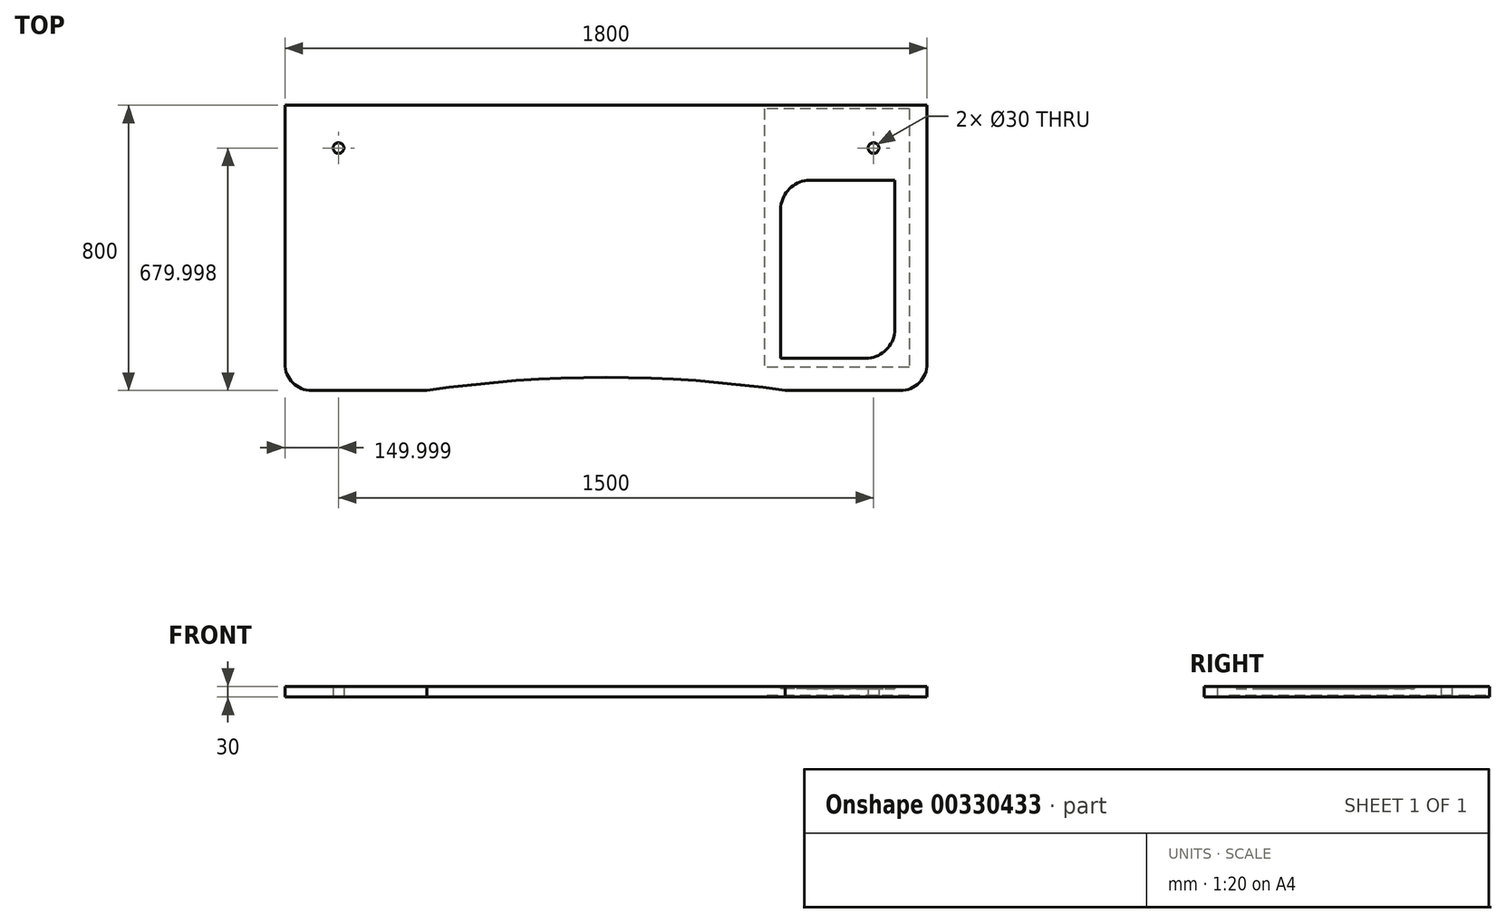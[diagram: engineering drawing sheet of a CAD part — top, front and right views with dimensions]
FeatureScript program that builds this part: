
annotation { "Feature Type Name" : "Feature", "Feature Type Description" : "" }
export const myFeature = defineFeature(function(context is Context, id is Id, definition is map)
    precondition{}
    {
        {
            var Q0;
            Q0=qCreatedBy(makeId("Top.planeOp"),FACE);
            var sketch = newSketch(context, id + "F0", { "sketchPlane" : qUnion([Q0])});
            skLineSegment(sketch, "E0.bottom", {"start": v(4430.2, -369.52) * mm, "end": v(4753.06, -369.52) * mm});
            skLineSegment(sketch, "E0.top", {"start": v(4355.2, 430.48) * mm, "end": v(6155.2, 430.48) * mm});
            skLineSegment(sketch, "E0.left", {"start": v(4355.2, -294.52) * mm, "end": v(4355.2, 430.48) * mm});
            skLineSegment(sketch, "E0.right", {"start": v(6155.2, -294.52) * mm, "end": v(6155.2, 430.48) * mm});
            skPoint(sketch, "E0.middle", {"position": v(5255.2, 30.48) * mm});
            skPoint(sketch, "E1.visualSharp", {"position": v(4355.2, -369.52) * mm});
            skArc(sketch, "E1.filletArc", {"start": v(4355.2, -294.52) * mm, "mid": v(4377.17, -347.55) * mm, "end": v(4430.2, -369.52) * mm});
            skPoint(sketch, "E2.visualSharp", {"position": v(6155.2, -369.52) * mm});
            skArc(sketch, "E2.filletArc", {"start": v(6080.2, -369.52) * mm, "mid": v(6133.23, -347.55) * mm, "end": v(6155.2, -294.52) * mm});
            skPoint(sketch, "E3", {"position": v(6155.2, 67.98) * mm});
            skLineSegment(sketch, "E4", {"start": v(6065.2, -195.15) * mm, "end": v(6065.2, 163.36) * mm});
            skLineSegment(sketch, "E5.3", {"start": v(6055.2, -204.44) * mm, "end": v(6055.2, 210.56) * mm});
            skPoint(sketch, "E6", {"position": v(4355.2, 310.48) * mm});
            skPoint(sketch, "E7", {"position": v(4505.2, 310.48) * mm});
            skLineSegment(sketch, "E8", {"start": v(5255.2, 30.48) * mm, "end": v(5255.2, 243.64) * mm, "construction": true});
            skCircle(sketch, "E9", {"center": v(4505.2, 310.48) * mm, "radius": 15 * mm});
            skCircle(sketch, "E10.MirrorC", {"center": v(6005.2, 310.48) * mm, "radius": 15 * mm});
            skLineSegment(sketch, "E11", {"start": v(5968, -279.52) * mm, "end": v(5990.2, -279.5) * mm});
            skLineSegment(sketch, "E12", {"start": v(6065.2, -204.44) * mm, "end": v(6065.2, -195.15) * mm});
            skPoint(sketch, "E13", {"position": v(6065.2, -204.44) * mm});
            skPoint(sketch, "E14", {"position": v(5990.2, -279.5) * mm});
            skPoint(sketch, "E15", {"position": v(5990.2, -269.22) * mm});
            skPoint(sketch, "E16", {"position": v(6055.2, -204.44) * mm});
            skPoint(sketch, "E17.orphan", {"position": v(6065.2, -279.44) * mm});
            skPoint(sketch, "E18", {"position": v(5755.2, -269.44) * mm});
            skLineSegment(sketch, "E19", {"start": v(5755.2, -269.44) * mm, "end": v(5755.2, 145.56) * mm});
            skPoint(sketch, "E20", {"position": v(5745.2, -279.52) * mm});
            skLineSegment(sketch, "E21", {"start": v(5968, -279.52) * mm, "end": v(5745.2, -279.52) * mm});
            skPoint(sketch, "E22", {"position": v(5755.2, 145.56) * mm});
            skLineSegment(sketch, "E23", {"start": v(5745.2, -279.52) * mm, "end": v(5745.2, 102.2) * mm});
            skLineSegment(sketch, "E24", {"start": v(6065.2, 163.36) * mm, "end": v(6065.2, 220.48) * mm});
            skPoint(sketch, "E25", {"position": v(6055.2, 210.56) * mm});
            skPoint(sketch, "E25.positionSnap0", {"position": v(6065.2, 210.56) * mm});
            skLineSegment(sketch, "E26", {"start": v(6055.2, 210.56) * mm, "end": v(5820.2, 210.56) * mm});
            skPoint(sketch, "E27", {"position": v(5820.2, 210.56) * mm});
            skArc(sketch, "E28", {"start": v(5820.2, 210.56) * mm, "mid": v(5776.63, 189.13) * mm, "end": v(5755.2, 145.56) * mm});
            skArc(sketch, "E29.0", {"start": v(5818.92, 220.48) * mm, "mid": v(5769.55, 196.2) * mm, "end": v(5745.28, 146.84) * mm});
            skLineSegment(sketch, "E30", {"start": v(5745.2, 102.2) * mm, "end": v(5745.28, 146.84) * mm});
            skLineSegment(sketch, "E31", {"start": v(5818.92, 220.48) * mm, "end": v(6065.2, 220.48) * mm});
            skLineSegment(sketch, "E32.trimOffspring", {"start": v(5757.33, -369.52) * mm, "end": v(6080.2, -369.52) * mm});
            skPoint(sketch, "E33.start.orphan", {"position": v(6055.2, -235.33) * mm});
            skLineSegment(sketch, "E34", {"start": v(5990.2, -269.22) * mm, "end": v(5755.2, -269.44) * mm});
            skPoint(sketch, "E35", {"position": v(5255.2, -332.65) * mm});
            skPoint(sketch, "E35.positionSnap0", {"position": v(5255.2, -333.31) * mm});
            skPoint(sketch, "E36.center.orphan", {"position": v(5255.2, -3833.31) * mm});
            skArc(sketch, "E37", {"start": v(5757.33, -369.52) * mm, "mid": v(5255.2, -332.65) * mm, "end": v(4753.06, -369.52) * mm});
            skArc(sketch, "E38", {"start": v(5990.2, -269.44) * mm, "mid": v(6033.77, -248.01) * mm, "end": v(6055.2, -204.44) * mm});
            skArc(sketch, "E39.0", {"start": v(5991.48, -279.36) * mm, "mid": v(6040.84, -255.08) * mm, "end": v(6065.12, -205.72) * mm});
            skLineSegment(sketch, "E40", {"start": v(6065.2, -204.44) * mm, "end": v(6065.12, -205.72) * mm});
            skLineSegment(sketch, "E41", {"start": v(5990.2, -279.5) * mm, "end": v(5991.48, -279.36) * mm});
            skSolve(sketch);
        }
        {
            var Q0;
            Q0=makeQuery(id+"F0.imprint","IMPRINT",FACE,{"disambiguationData":[TD([[makeQuery(id+"F0.imprint","IMPRINT",EDGE,{"derivedFrom":sQuery(id+"F0.wireOp",EDGE,"E0.top")}),-1.0]])]});
            var Q1;
            {var subQ3=sQuery(id+"F0.wireOp",EDGE,"WvALyXb5-F5Po-nu7d-ekky-OqId0BbYu9Vm");Q1=makeQuery(id+"F0.imprint","IMPRINT",FACE,{"disambiguationData":[TD([[makeQuery(id+"F0.imprint","IMPRINT",EDGE,{"derivedFrom":subQ3}),-1.0]])]});}
            extrude(context, id + "F1", {"entities" : qUnion([Q0, Q1]), "depth" : 30 * mm});
        }
        {
            var Q0;
            Q0=makeQuery(id+"F0.imprint","IMPRINT",FACE,{"disambiguationData":[TD([[makeQuery(id+"F0.imprint","IMPRINT",EDGE,{"derivedFrom":sQuery(id+"F0.wireOp",EDGE,"E4")}),1.0]])]});
            extrude(context, id + "F2", {"entities" : qUnion([Q0]), "operationType" : NewBodyOperationType.ADD, "depth" : 24 * mm});
        }
        {
            var Q0;
            Q0=makeQuery(id+"F0.imprint","IMPRINT",FACE,{"disambiguationData":[TD([[makeQuery(id+"F0.imprint","IMPRINT",EDGE,{"derivedFrom":sQuery(id+"F0.wireOp",EDGE,"E0.top")}),-1.0]])]});
            var sketch = newSketch(context, id + "F3", { "sketchPlane" : qUnion([Q0])});
            skPoint(sketch, "E42", {"position": v(6105.2, 420.48) * mm});
            skLineSegment(sketch, "E43.bottom", {"start": v(6105.2, 420.48) * mm, "end": v(5699.2, 420.48) * mm});
            skLineSegment(sketch, "E43.top", {"start": v(6105.2, -304.52) * mm, "end": v(5699.2, -304.52) * mm});
            skLineSegment(sketch, "E43.left", {"start": v(6105.2, 420.48) * mm, "end": v(6105.2, -304.52) * mm});
            skLineSegment(sketch, "E43.right", {"start": v(5699.2, 420.48) * mm, "end": v(5699.2, -304.52) * mm});
            skPoint(sketch, "E44", {"position": v(4821.67, -299.11) * mm});
            skSolve(sketch);
        }
        {
            var Q0;
            Q0=makeQuery(id+"F3.imprint","IMPRINT",FACE,{"disambiguationData":[TD([[makeQuery(id+"F3.imprint","IMPRINT",EDGE,{"derivedFrom":sQuery(id+"F3.wireOp",EDGE,"E43.bottom")}),1.0]])]});
            var Q1;
            Q1=makeQuery(id+"F0.imprint","IMPRINT",FACE,{"disambiguationData":[TD([[makeQuery(id+"F0.imprint","IMPRINT",EDGE,{"derivedFrom":sQuery(id+"F0.wireOp",EDGE,"E4")}),1.0]])]});
            extrude(context, id + "F4", {"entities" : qUnion([Q0, Q1]), "operationType" : NewBodyOperationType.REMOVE, "depth" : 4 * mm, "offsetDistance" : 25 * mm});
        }
    });
